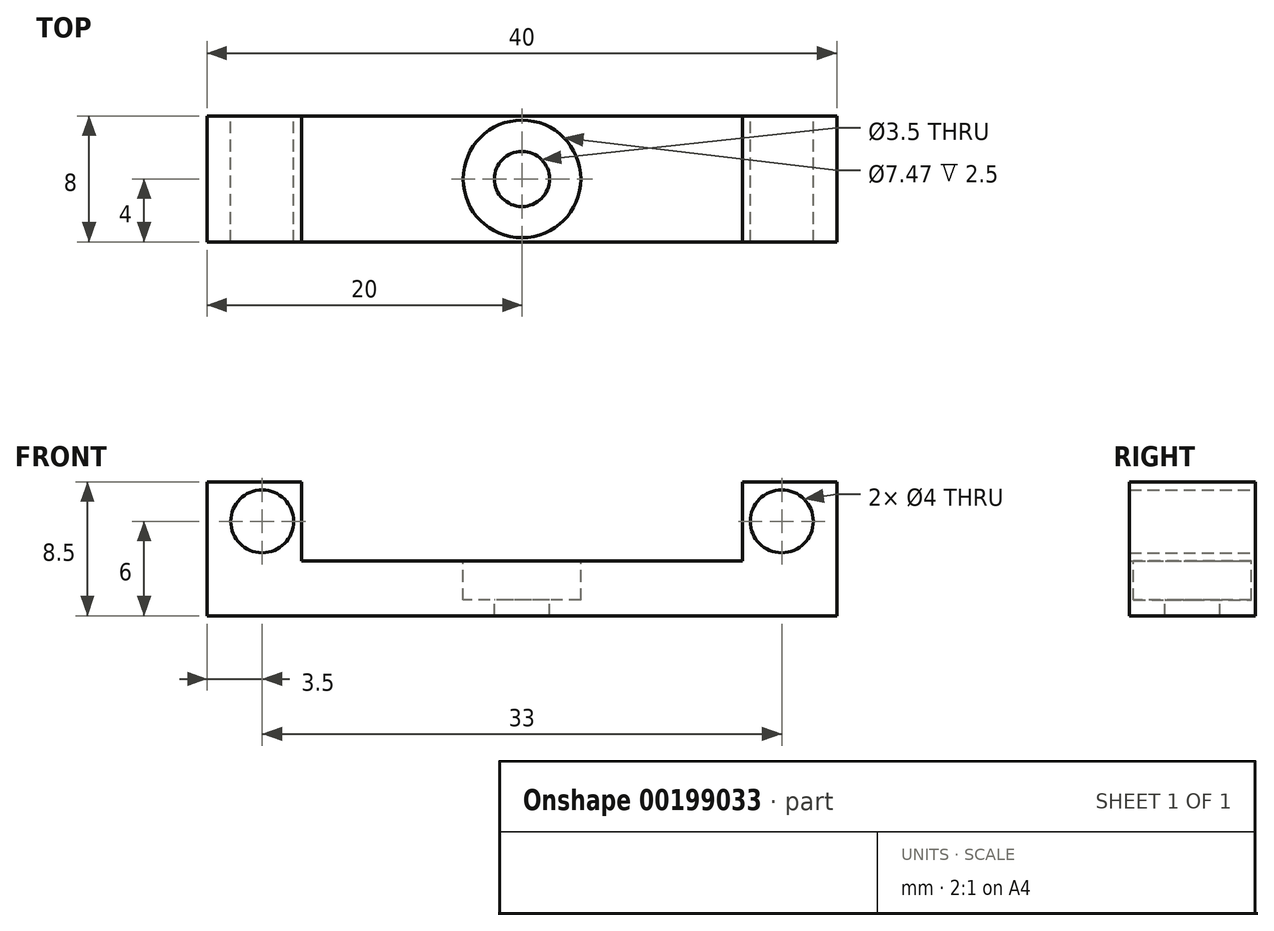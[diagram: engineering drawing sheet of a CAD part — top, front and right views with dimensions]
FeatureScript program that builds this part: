
annotation { "Feature Type Name" : "Feature", "Feature Type Description" : "" }
export const myFeature = defineFeature(function(context is Context, id is Id, definition is map)
    precondition{}
    {
        {
            var Q0;
            Q0=qCreatedBy(makeId("Front.planeOp"),FACE);
            var sketch = newSketch(context, id + "F0", { "sketchPlane" : qUnion([Q0])});
            skLineSegment(sketch, "E0.bottom", {"start": v(20, 1.75) * mm, "end": v(-20, 1.75) * mm});
            skLineSegment(sketch, "E0.top", {"start": v(20, -1.75) * mm, "end": v(-20, -1.75) * mm});
            skLineSegment(sketch, "E0.left", {"start": v(20, 1.75) * mm, "end": v(20, -1.75) * mm});
            skLineSegment(sketch, "E0.right", {"start": v(-20, 1.75) * mm, "end": v(-20, -1.75) * mm});
            skPoint(sketch, "E0.middle", {"position": v(0, 0) * mm});
            skLineSegment(sketch, "E1.bottom", {"start": v(-20, 1.75) * mm, "end": v(-14, 1.75) * mm});
            skLineSegment(sketch, "E1.top", {"start": v(-20, 6.75) * mm, "end": v(-14, 6.75) * mm});
            skLineSegment(sketch, "E1.left", {"start": v(-20, 1.75) * mm, "end": v(-20, 6.75) * mm});
            skLineSegment(sketch, "E1.right", {"start": v(-14, 1.75) * mm, "end": v(-14, 6.75) * mm});
            skLineSegment(sketch, "E2.bottom", {"start": v(20, 1.75) * mm, "end": v(14, 1.75) * mm});
            skLineSegment(sketch, "E2.top", {"start": v(20, 6.75) * mm, "end": v(14, 6.75) * mm});
            skLineSegment(sketch, "E2.left", {"start": v(20, 1.75) * mm, "end": v(20, 6.75) * mm});
            skLineSegment(sketch, "E2.right", {"start": v(14, 1.75) * mm, "end": v(14, 6.75) * mm});
            skLineSegment(sketch, "E3", {"start": v(0, 0) * mm, "end": v(16.5, 0) * mm});
            skLineSegment(sketch, "E4", {"start": v(0, 0) * mm, "end": v(-16.5, 0) * mm});
            skLineSegment(sketch, "E5", {"start": v(-20, 4.25) * mm, "end": v(-14, 4.25) * mm});
            skLineSegment(sketch, "E6", {"start": v(14, 4.25) * mm, "end": v(20, 4.25) * mm});
            skLineSegment(sketch, "E7", {"start": v(-16.5, 0) * mm, "end": v(-16.5, 4.25) * mm});
            skLineSegment(sketch, "E8", {"start": v(16.5, 0) * mm, "end": v(16.5, 4.25) * mm});
            skCircle(sketch, "E9", {"center": v(-16.5, 4.25) * mm, "radius": 2 * mm});
            skCircle(sketch, "E10", {"center": v(16.5, 4.25) * mm, "radius": 2 * mm});
            skSolve(sketch);
        }
        {
            var Q0;
            Q0 = qSketchRegion(id + "F0", true);
            extrude(context, id + "F1", {"entities" : qUnion([Q0]), "depth" : 8 * mm});
        }
        {
            var Q0;
            Q0=makeQuery(id+"F1.opExtrude","SWEPT_FACE",FACE,{"disambiguationData":[OSD([sQuery(id+"F0.wireOp",EDGE,"E0.bottom")])]});
            var sketch = newSketch(context, id + "F2", { "sketchPlane" : qUnion([Q0])});
            skLineSegment(sketch, "E11", {"start": v(0, 0) * mm, "end": v(0, -4) * mm});
            skPoint(sketch, "E11.endSnap0", {"position": v(0, 0) * mm});
            skCircle(sketch, "E12", {"center": v(0, -4) * mm, "radius": 1.75 * mm});
            skSolve(sketch);
        }
        {
            var Q0;
            Q0=makeQuery(id+"F2.imprint","IMPRINT",FACE,{"disambiguationData":[TD([[makeQuery(id+"F2.imprint","IMPRINT",EDGE,{"derivedFrom":sQuery(id+"F2.wireOp",EDGE,"E12")}),1.0]])]});
            extrude(context, id + "F3", {"entities" : qUnion([Q0]), "operationType" : NewBodyOperationType.REMOVE, "oppositeDirection" : true, "depth" : 25 * mm});
        }
        {
            var Q0;
            Q0=makeQuery(id+"F1.opExtrude","SWEPT_FACE",FACE,{"disambiguationData":[OSD([sQuery(id+"F0.wireOp",EDGE,"E0.bottom")])]});
            var sketch = newSketch(context, id + "F4", { "sketchPlane" : qUnion([Q0])});
            skCircle(sketch, "E13", {"center": v(0, -4) * mm, "radius": 3.73 * mm});
            skSolve(sketch);
        }
        {
            var Q0;
            Q0=makeQuery(id+"F4.imprint","IMPRINT",FACE,{"disambiguationData":[TD([[makeQuery(id+"F4.imprint","IMPRINT",EDGE,{"derivedFrom":sQuery(id+"F4.wireOp",EDGE,"E13")}),1.0]])]});
            extrude(context, id + "F5", {"entities" : qUnion([Q0]), "operationType" : NewBodyOperationType.REMOVE, "oppositeDirection" : true, "depth" : 2.5 * mm});
        }
    });
